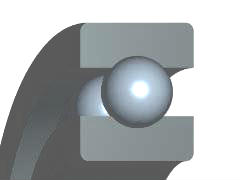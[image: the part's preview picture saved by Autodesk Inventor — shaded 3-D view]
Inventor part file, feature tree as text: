
AUTODESK INVENTOR PART (.ipt)
format: ipt  version: 2019 (Build 230136000, 136)  size: 459,264 bytes
history: native  units: mm (DEFAULTED — no unit token found)
features: other x3, plane x2, pattern_circular x1
ambient origin geometry x8: Origin, YZ Plane, XZ Plane, XY Plane, X Axis, Y Axis, Z Axis, Center Point
bodies: Solid1 (feature_tree)
feature tree (6):
  other  "WorkPoint1"
  other  "WorkAxis1"
  plane  "WorkPlane3"
  plane  "WorkPlane4"
  other  "WorkPoint2"
  pattern_circular  "Seriepolare1"  Count=2  [1 undecoded]
note: 1 required parameter value undecoded (feature->parameter linkage not recoverable at this tier; creation-order binding heuristic only, values carry confidence <= 0.55)
